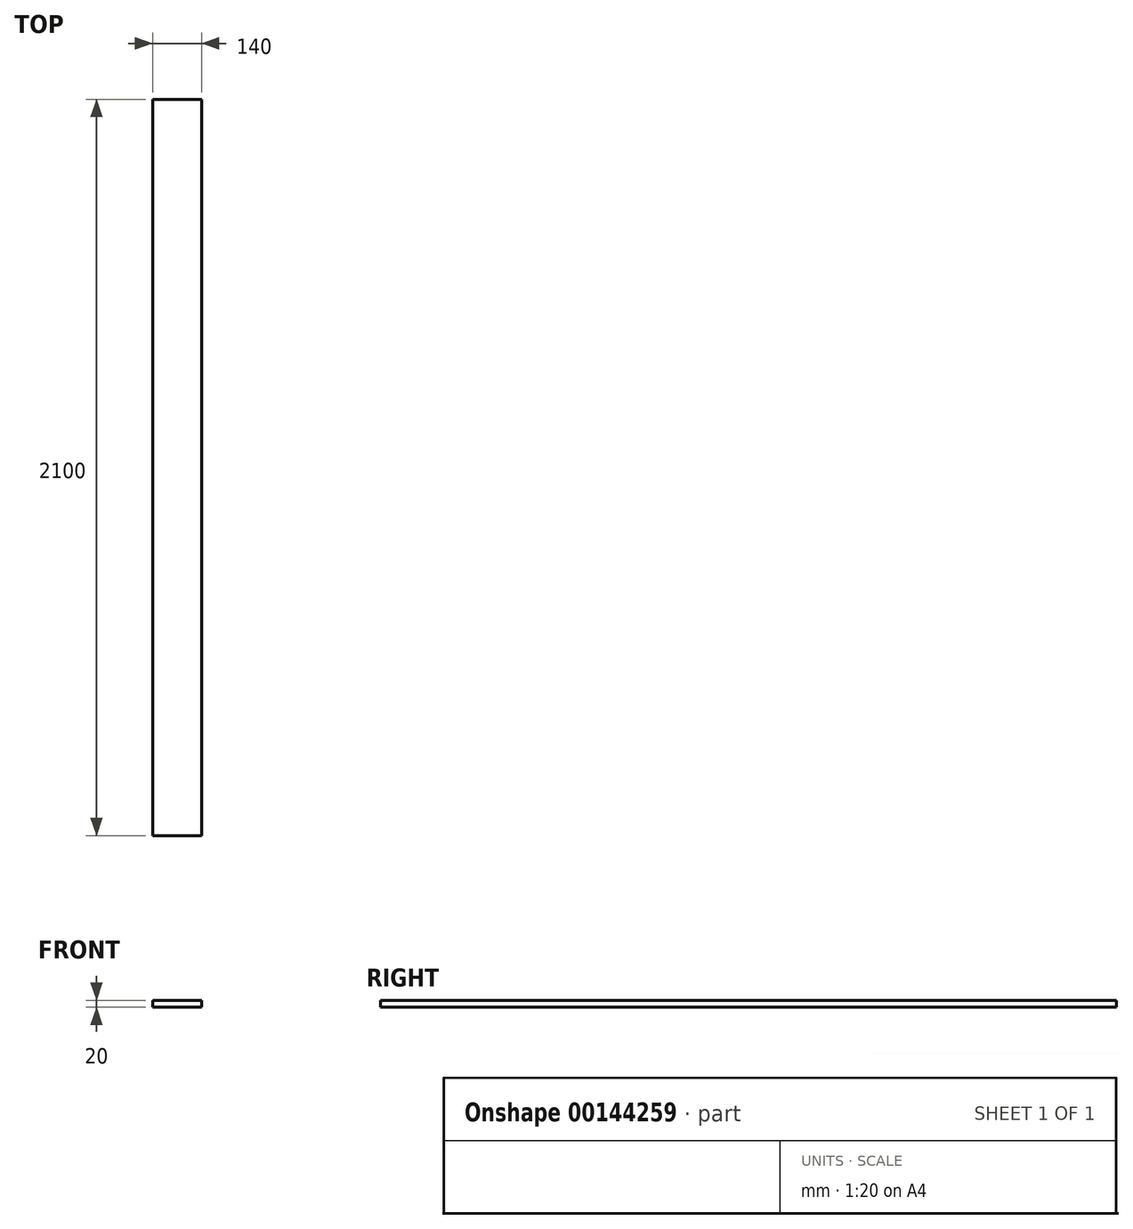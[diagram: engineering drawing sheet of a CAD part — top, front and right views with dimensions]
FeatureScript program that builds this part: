
annotation { "Feature Type Name" : "Feature", "Feature Type Description" : "" }
export const myFeature = defineFeature(function(context is Context, id is Id, definition is map)
    precondition{}
    {
        {
            var Q0;
            Q0=qCreatedBy(makeId("Front.planeOp"),FACE);
            var sketch = newSketch(context, id + "F0", { "sketchPlane" : qUnion([Q0])});
            skLineSegment(sketch, "E0.bottom", {"start": v(0, 0) * mm, "end": v(140, 0) * mm});
            skLineSegment(sketch, "E0.top", {"start": v(0, 20) * mm, "end": v(140, 20) * mm});
            skLineSegment(sketch, "E0.left", {"start": v(0, 0) * mm, "end": v(0, 20) * mm});
            skLineSegment(sketch, "E0.right", {"start": v(140, 0) * mm, "end": v(140, 20) * mm});
            skSolve(sketch);
        }
        {
            var Q0;
            Q0=makeQuery(id+"F0.imprint","IMPRINT",FACE,{"disambiguationData":[TD([[makeQuery(id+"F0.imprint","IMPRINT",EDGE,{"derivedFrom":sQuery(id+"F0.wireOp",EDGE,"E0.bottom")}),1.0]])]});
            extrude(context, id + "F1", {"entities" : qUnion([Q0]), "depth" : 2100 * mm});
        }
    });
